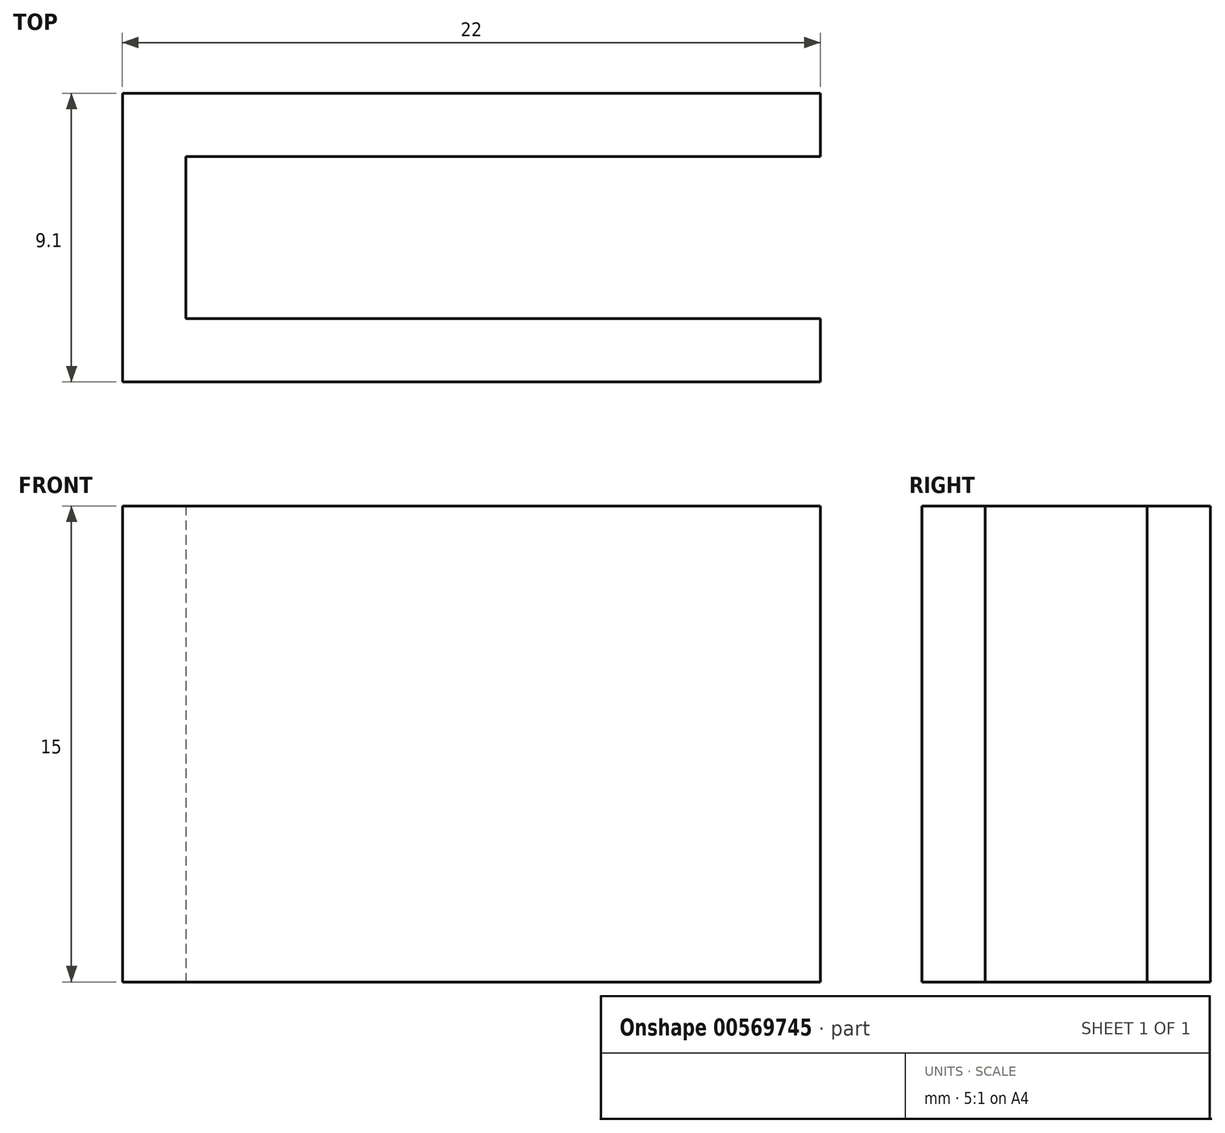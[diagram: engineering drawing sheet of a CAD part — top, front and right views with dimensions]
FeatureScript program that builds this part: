
annotation { "Feature Type Name" : "Feature", "Feature Type Description" : "" }
export const myFeature = defineFeature(function(context is Context, id is Id, definition is map)
    precondition{}
    {
        {
            var Q0;
            Q0=qCreatedBy(makeId("Top.planeOp"),FACE);
            var sketch = newSketch(context, id + "F0", { "sketchPlane" : qUnion([Q0])});
            skLineSegment(sketch, "E0", {"start": v(-11.96, 3.73) * mm, "end": v(10.04, 3.73) * mm});
            skLineSegment(sketch, "E1", {"start": v(-11.96, 3.73) * mm, "end": v(-11.96, -5.37) * mm});
            skLineSegment(sketch, "E2", {"start": v(-11.96, -5.37) * mm, "end": v(10.04, -5.37) * mm});
            skLineSegment(sketch, "E3", {"start": v(10.04, -5.37) * mm, "end": v(10.04, -3.37) * mm});
            skLineSegment(sketch, "E4", {"start": v(10.04, -3.37) * mm, "end": v(-9.96, -3.37) * mm});
            skLineSegment(sketch, "E5", {"start": v(-9.96, -3.37) * mm, "end": v(-9.96, 1.73) * mm});
            skLineSegment(sketch, "E6", {"start": v(-9.96, 1.73) * mm, "end": v(10.04, 1.73) * mm});
            skLineSegment(sketch, "E7", {"start": v(10.04, 3.73) * mm, "end": v(10.04, 1.73) * mm});
            skSolve(sketch);
        }
        {
            var Q0;
            Q0 = qSketchRegion(id + "F0", true);
            extrude(context, id + "F1", {"entities" : qUnion([Q0]), "depth" : 15 * mm, "offsetDistance" : 25 * mm});
        }
    });
